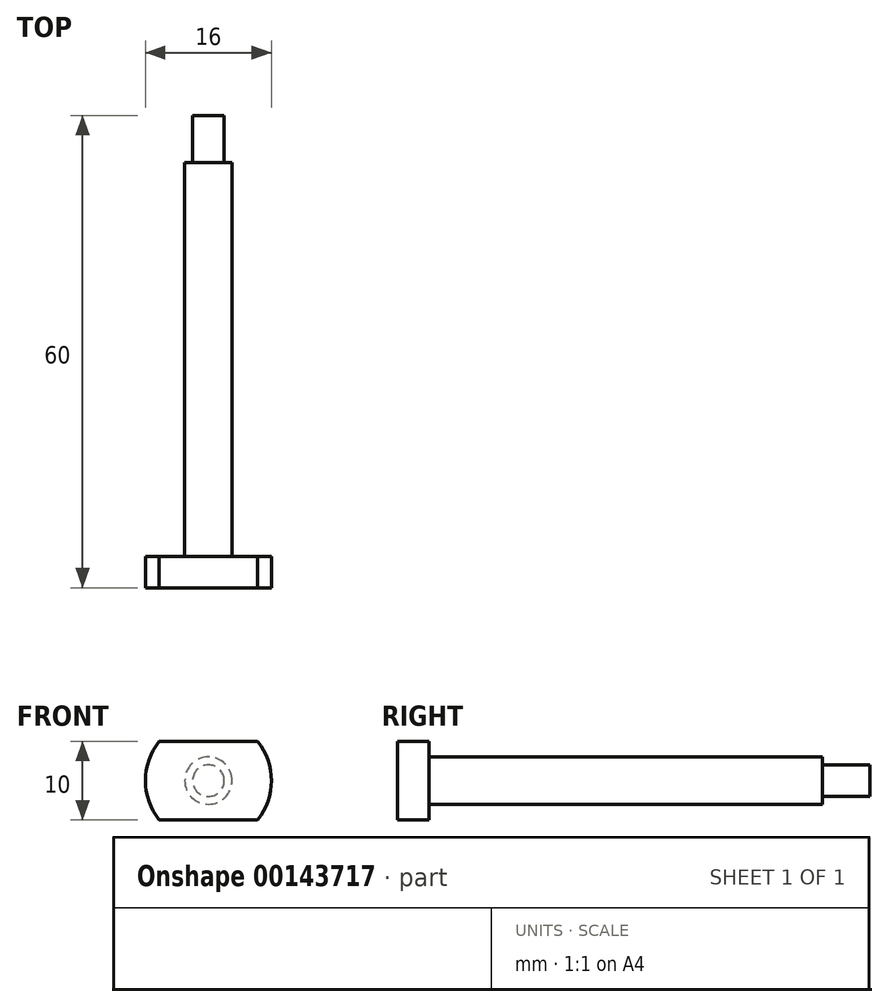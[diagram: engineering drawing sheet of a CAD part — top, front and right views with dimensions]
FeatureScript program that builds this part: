
annotation { "Feature Type Name" : "Feature", "Feature Type Description" : "" }
export const myFeature = defineFeature(function(context is Context, id is Id, definition is map)
    precondition{}
    {
        {
            var Q0;
            Q0=qCreatedBy(makeId("Right.planeOp"),FACE);
            var sketch = newSketch(context, id + "F0", { "sketchPlane" : qUnion([Q0])});
            skLineSegment(sketch, "E0", {"start": v(-89.47, 0) * mm, "end": v(-89.47, 8) * mm});
            skLineSegment(sketch, "E1", {"start": v(-89.47, 8) * mm, "end": v(-85.47, 8) * mm});
            skLineSegment(sketch, "E2", {"start": v(-85.47, 8) * mm, "end": v(-85.47, 3) * mm});
            skLineSegment(sketch, "E3", {"start": v(-85.47, 3) * mm, "end": v(-35.47, 3) * mm});
            skLineSegment(sketch, "E4", {"start": v(-35.47, 3) * mm, "end": v(-35.47, 2) * mm});
            skLineSegment(sketch, "E5", {"start": v(-35.47, 2) * mm, "end": v(-29.47, 2) * mm});
            skLineSegment(sketch, "E6", {"start": v(-29.47, 2) * mm, "end": v(-29.47, 0) * mm});
            skLineSegment(sketch, "E7", {"start": v(-89.47, 0) * mm, "end": v(-29.47, 0) * mm});
            skSolve(sketch);
        }
        {
            var Q0;
            Q0=qCreatedBy(makeId("Right.planeOp"),FACE);
            var sketch = newSketch(context, id + "F1", { "sketchPlane" : qUnion([Q0])});
            skLineSegment(sketch, "E8", {"start": v(-99.5, 0) * mm, "end": v(-21.04, 0) * mm, "construction": true});
            skSolve(sketch);
        }
        {
            var Q0;
            Q0 = qSketchRegion(id + "F0", true);
            var Q1;
            Q1=sQuery(id+"F1.wireOp",EDGE,"E8");
            revolve(context, id + "F2", {"entities" : qUnion([Q0]), "axis" : qUnion([Q1]), "revolveType" : RevolveType.FULL});
        }
        {
            var Q0;
            Q0=makeQuery(id+"F2.opRevolve","SWEPT_FACE",FACE,{"disambiguationData":[OSD([sQuery(id+"F0.wireOp",EDGE,"E0")])]});
            var sketch = newSketch(context, id + "F3", { "sketchPlane" : qUnion([Q0])});
            skLineSegment(sketch, "E9", {"start": v(-9.32, 5) * mm, "end": v(9.77, 5) * mm});
            skLineSegment(sketch, "E10", {"start": v(9.77, -5) * mm, "end": v(-9.32, -5) * mm});
            skLineSegment(sketch, "E11", {"start": v(-9.32, -5) * mm, "end": v(-9.32, -9.75) * mm});
            skLineSegment(sketch, "E12", {"start": v(-9.32, -9.75) * mm, "end": v(9.77, -9.75) * mm});
            skLineSegment(sketch, "E13", {"start": v(9.77, 9.93) * mm, "end": v(-9.32, 9.93) * mm});
            skLineSegment(sketch, "E14", {"start": v(-9.32, 9.93) * mm, "end": v(-9.32, 5) * mm});
            skLineSegment(sketch, "E15", {"start": v(9.77, 5) * mm, "end": v(9.77, 9.93) * mm});
            skLineSegment(sketch, "E16", {"start": v(9.77, -5) * mm, "end": v(9.77, -9.75) * mm});
            skSolve(sketch);
        }
        {
            var Q0;
            Q0 = qSketchRegion(id + "F3", true);
            extrude(context, id + "F4", {"entities" : qUnion([Q0]), "operationType" : NewBodyOperationType.REMOVE, "endBound" : BoundingType.UP_TO_NEXT, "oppositeDirection" : true, "depth" : 25 * mm});
        }
    });
